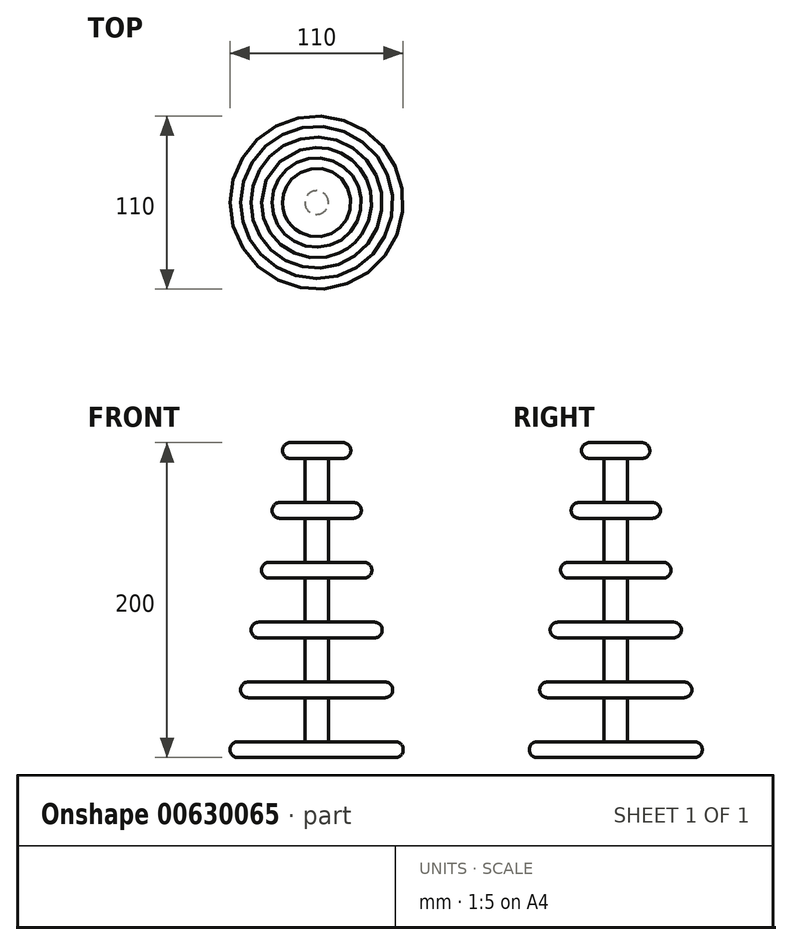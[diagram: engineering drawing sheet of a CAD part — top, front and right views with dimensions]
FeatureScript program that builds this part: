
annotation { "Feature Type Name" : "Feature", "Feature Type Description" : "" }
export const myFeature = defineFeature(function(context is Context, id is Id, definition is map)
    precondition{}
    {
        {
            var Q0;
            Q0=qCreatedBy(makeId("Front.planeOp"),FACE);
            var sketch = newSketch(context, id + "F0", { "sketchPlane" : qUnion([Q0])});
            skLineSegment(sketch, "E0.bottom", {"start": v(-30.05, 14) * mm, "end": v(0, 14) * mm});
            skLineSegment(sketch, "E0.top", {"start": v(-28.3, 24) * mm, "end": v(0, 24) * mm});
            skPoint(sketch, "E0.middle", {"position": v(0, 19) * mm});
            skLineSegment(sketch, "E1.top", {"start": v(-41.6, -52) * mm, "end": v(0, -52) * mm});
            skPoint(sketch, "E1.middle", {"position": v(0, -57) * mm});
            skPoint(sketch, "E1.middle.positionSnap0", {"position": v(0, 14) * mm});
            skLineSegment(sketch, "E2.bottom", {"start": v(-50, -100) * mm, "end": v(0, -100) * mm});
            skLineSegment(sketch, "E2.top", {"start": v(-50, -90) * mm, "end": v(0, -90) * mm});
            skPoint(sketch, "E2.middle", {"position": v(0, -95) * mm});
            skPoint(sketch, "E2.middle.positionSnap0", {"position": v(0, -62) * mm});
            skLineSegment(sketch, "E3", {"start": v(-239.36, 0) * mm, "end": v(-179.84, 0) * mm, "construction": true});
            skPoint(sketch, "E4.MirrorP", {"position": v(0, -14) * mm});
            skPoint(sketch, "E5.MirrorP", {"position": v(0, -19) * mm});
            skPoint(sketch, "E6.MirrorP", {"position": v(0, 57) * mm});
            skLineSegment(sketch, "E7.MirrorCS", {"start": v(-16.75, 90) * mm, "end": v(0, 90) * mm});
            skLineSegment(sketch, "E8.MirrorCS", {"start": v(-15, 100) * mm, "end": v(0, 100) * mm});
            skLineSegment(sketch, "E9.MirrorCS", {"start": v(-34.95, -14) * mm, "end": v(0, -14) * mm});
            skPoint(sketch, "E10.MirrorP", {"position": v(0, 95) * mm});
            skPoint(sketch, "E11.MirrorP", {"position": v(0, 62) * mm});
            skLineSegment(sketch, "E12.MirrorCS", {"start": v(-23.4, 52) * mm, "end": v(0, 52) * mm});
            skLineSegment(sketch, "E13.MirrorCS", {"start": v(-21.65, 62) * mm, "end": v(0, 62) * mm});
            skLineSegment(sketch, "E14", {"start": v(0, 136.2) * mm, "end": v(0, 180.6) * mm, "construction": true});
            skLineSegment(sketch, "E15", {"start": v(-36.7, -24) * mm, "end": v(0, -24) * mm});
            skArc(sketch, "E16", {"start": v(-50, -90) * mm, "mid": v(-55, -95) * mm, "end": v(-50, -100) * mm});
            skArc(sketch, "E17", {"start": v(-43.35, -52) * mm, "mid": v(-48.35, -57) * mm, "end": v(-43.35, -62) * mm});
            skArc(sketch, "E18", {"start": v(-36.7, -14) * mm, "mid": v(-41.7, -19) * mm, "end": v(-36.7, -24) * mm});
            skArc(sketch, "E19", {"start": v(-30.05, 24) * mm, "mid": v(-35.05, 19) * mm, "end": v(-30.05, 14) * mm});
            skArc(sketch, "E20", {"start": v(-23.4, 62) * mm, "mid": v(-28.4, 57) * mm, "end": v(-23.4, 52) * mm});
            skArc(sketch, "E21", {"start": v(-16.75, 100) * mm, "mid": v(-21.75, 95) * mm, "end": v(-16.75, 90) * mm});
            skLineSegment(sketch, "E22", {"start": v(-16.75, 100) * mm, "end": v(-15, 100) * mm});
            skLineSegment(sketch, "E23", {"start": v(-21.65, 62) * mm, "end": v(-23.4, 62) * mm});
            skLineSegment(sketch, "E24", {"start": v(-30.05, 24) * mm, "end": v(-28.3, 24) * mm});
            skLineSegment(sketch, "E25", {"start": v(-36.7, -14) * mm, "end": v(-34.95, -14) * mm});
            skLineSegment(sketch, "E26", {"start": v(-43.35, -52) * mm, "end": v(-41.6, -52) * mm});
            skLineSegment(sketch, "E27", {"start": v(0, 100) * mm, "end": v(0, 90) * mm});
            skPoint(sketch, "E28.orphan", {"position": v(50, -100) * mm});
            skPoint(sketch, "E29.orphan", {"position": v(50, -90) * mm});
            skPoint(sketch, "E30.orphan", {"position": v(15, 100) * mm});
            skLineSegment(sketch, "E31.trimOffspring", {"start": v(0, 62) * mm, "end": v(0, 52) * mm});
            skLineSegment(sketch, "E32.trimOffspring", {"start": v(0, 24) * mm, "end": v(0, 14) * mm});
            skLineSegment(sketch, "E33.trimOffspring", {"start": v(0, -14) * mm, "end": v(0, -24) * mm});
            skLineSegment(sketch, "E34.trimOffspring", {"start": v(0, -52) * mm, "end": v(0, -62) * mm});
            skLineSegment(sketch, "E35.trimOffspring", {"start": v(0, -90) * mm, "end": v(0, -100) * mm});
            skLineSegment(sketch, "E36", {"start": v(-43.35, -62) * mm, "end": v(0, -62) * mm});
            skSolve(sketch);
        }
        {
            var Q0;
            Q0 = qSketchRegion(id + "F0", true);
            var Q1;
            Q1=sQuery(id+"F0.wireOp",EDGE,"E14");
            revolve(context, id + "F1", {"entities" : qUnion([Q0]), "axis" : qUnion([Q1]), "revolveType" : RevolveType.FULL});
        }
        {
            var Q0;
            Q0=makeQuery(id+"F1.opRevolve","SWEPT_FACE",FACE,{"disambiguationData":[OSD([sQuery(id+"F0.wireOp",EDGE,"E8.MirrorCS"),sQuery(id+"F0.wireOp",EDGE,"E22")])]});
            var sketch = newSketch(context, id + "F2", { "sketchPlane" : qUnion([Q0])});
            skCircle(sketch, "E37", {"center": v(0, 0) * mm, "radius": 7.5 * mm});
            skSolve(sketch);
        }
        {
            var Q0;
            Q0 = qSketchRegion(id + "F2", true);
            var Q1;
            Q1=makeQuery(id+"F1.opRevolve","SWEPT_FACE",FACE,{"disambiguationData":[OSD([sQuery(id+"F0.wireOp",EDGE,"E2.bottom")])]});
            extrude(context, id + "F3", {"entities" : qUnion([Q0]), "operationType" : NewBodyOperationType.ADD, "endBound" : BoundingType.UP_TO_SURFACE, "oppositeDirection" : true, "depth" : 25 * mm, "endBoundEntityFace" : qUnion([Q1]), "offsetDistance" : 25 * mm});
        }
    });
